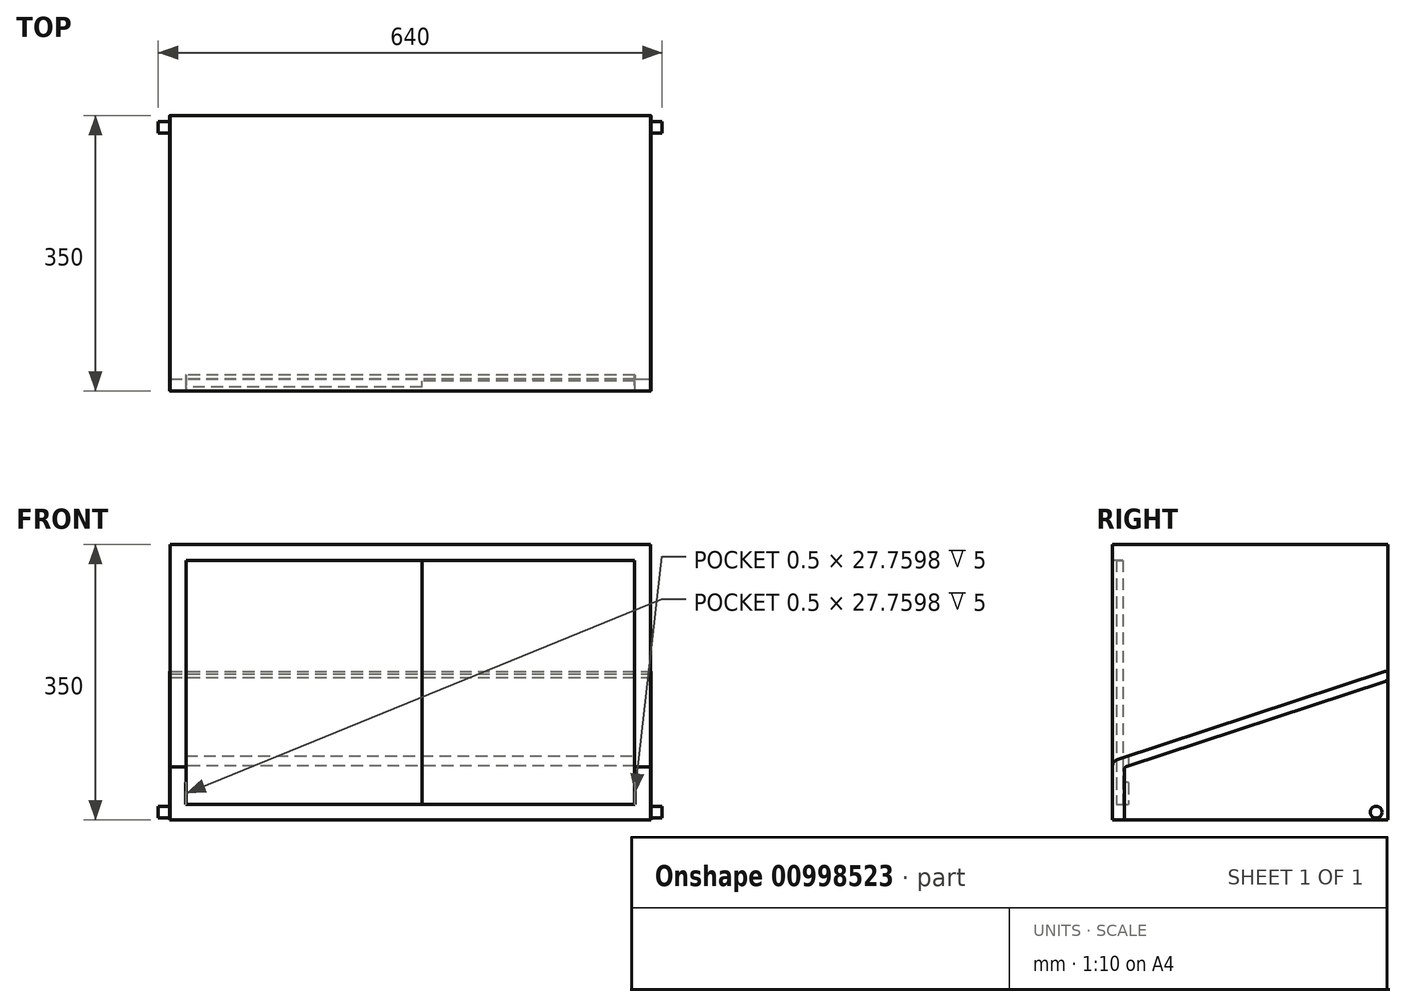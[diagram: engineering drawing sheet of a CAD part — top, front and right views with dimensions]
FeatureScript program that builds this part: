
annotation { "Feature Type Name" : "Feature", "Feature Type Description" : "" }
export const myFeature = defineFeature(function(context is Context, id is Id, definition is map)
    precondition{}
    {
        {
            var Q0;
            Q0=qCreatedBy(makeId("Right.planeOp"),FACE);
            var sketch = newSketch(context, id + "F0", { "sketchPlane" : qUnion([Q0])});
            skLineSegment(sketch, "E0.bottom", {"start": v(0, 0) * mm, "end": v(-350, 0) * mm});
            skLineSegment(sketch, "E0.top", {"start": v(0, 350) * mm, "end": v(-350, 350) * mm});
            skLineSegment(sketch, "E0.left", {"start": v(0, 0) * mm, "end": v(0, 350) * mm});
            skLineSegment(sketch, "E0.right", {"start": v(-350, 0) * mm, "end": v(-350, 350) * mm});
            skPoint(sketch, "E0.middle", {"position": v(-175, 175) * mm});
            skLineSegment(sketch, "E1", {"start": v(-350, 0) * mm, "end": v(-350, 67.76) * mm});
            skLineSegment(sketch, "E2", {"start": v(-343.12, 77.26) * mm, "end": v(-3.94, 188.7) * mm});
            skLineSegment(sketch, "E3", {"start": v(0, 185.86) * mm, "end": v(0, 180.99) * mm});
            skLineSegment(sketch, "E4", {"start": v(-3.44, 176.24) * mm, "end": v(-331.56, 68.43) * mm});
            skLineSegment(sketch, "E5", {"start": v(-335, 63.68) * mm, "end": v(-335, 0) * mm});
            skLineSegment(sketch, "E6", {"start": v(-335, 0) * mm, "end": v(-350, 0) * mm});
            skPoint(sketch, "E7.visualSharp", {"position": v(-350, 75) * mm});
            skArc(sketch, "E7.filletArc", {"start": v(-343.12, 77.26) * mm, "mid": v(-348.1, 73.62) * mm, "end": v(-350, 67.76) * mm});
            skPoint(sketch, "E8.visualSharp", {"position": v(-335, 67.3) * mm});
            skArc(sketch, "E8.filletArc", {"start": v(-331.56, 68.43) * mm, "mid": v(-334.05, 66.6) * mm, "end": v(-335, 63.68) * mm});
            skPoint(sketch, "E9.visualSharp", {"position": v(0, 177.37) * mm});
            skArc(sketch, "E9.filletArc", {"start": v(-3.44, 176.24) * mm, "mid": v(-0.95, 178.06) * mm, "end": v(0, 180.99) * mm});
            skPoint(sketch, "E10.visualSharp", {"position": v(0, 190) * mm});
            skArc(sketch, "E10.filletArc", {"start": v(0, 185.86) * mm, "mid": v(-1.24, 188.29) * mm, "end": v(-3.94, 188.7) * mm});
            skSolve(sketch);
        }
        {
            var Q0;
            {var subQ0=sQuery(id+"F0.wireOp",EDGE,"E0.bottom");Q0=makeQuery(id+"F0.imprint","IMPRINT",FACE,{"disambiguationData":[TD([[makeQuery(id+"F0.imprint","IMPRINT",EDGE,{"derivedFrom":subQ0}),-1.0]])]});}
            var Q1;
            {var subQ5=sQuery(id+"F0.wireOp",EDGE,"E6");Q1=makeQuery(id+"F0.imprint","IMPRINT",FACE,{"disambiguationData":[TD([[makeQuery(id+"F0.imprint","IMPRINT",EDGE,{"derivedFrom":subQ5}),-1.0]])]});}
            var Q2;
            {var subQ1=sQuery(id+"F0.wireOp",EDGE,"E0.top");Q2=makeQuery(id+"F0.imprint","IMPRINT",FACE,{"disambiguationData":[TD([[makeQuery(id+"F0.imprint","IMPRINT",EDGE,{"derivedFrom":subQ1}),1.0]])]});}
            extrude(context, id + "F1", {"entities" : qUnion([Q0, Q1, Q2]), "depth" : 305 * mm, "offsetDistance" : 25 * mm});
        }
        {
            var Q0;
            Q0=makeQuery(id+"F1.opExtrude","CAP_FACE",FACE,{"disambiguationData":[OSD([sQuery(id+"F0.wireOp",EDGE,"E0.bottom"),sQuery(id+"F0.wireOp",EDGE,"E0.top"),sQuery(id+"F0.wireOp",EDGE,"E0.left"),sQuery(id+"F0.wireOp",EDGE,"E1"),sQuery(id+"F0.wireOp",EDGE,"E6")])],"isStart":false});
            var sketch = newSketch(context, id + "F2", { "sketchPlane" : qUnion([Q0])});
            skLineSegment(sketch, "E11.0.0", {"start": v(-3.94, 188.7) * mm, "end": v(-343.12, 77.26) * mm});
            skArc(sketch, "E11.0.1", {"start": v(-343.12, 77.26) * mm, "mid": v(-348.1, 73.62) * mm, "end": v(-350, 67.76) * mm});
            skLineSegment(sketch, "E11.0.2", {"start": v(-350, 67.76) * mm, "end": v(-350, 67.76) * mm});
            skLineSegment(sketch, "E11.0.4", {"start": v(-335, 63.68) * mm, "end": v(-335, 63.68) * mm});
            skArc(sketch, "E11.0.5", {"start": v(-335, 63.68) * mm, "mid": v(-334.05, 66.6) * mm, "end": v(-331.56, 68.43) * mm});
            skLineSegment(sketch, "E11.0.6", {"start": v(-331.56, 68.43) * mm, "end": v(-3.44, 176.24) * mm});
            skArc(sketch, "E11.0.7", {"start": v(-3.44, 176.24) * mm, "mid": v(-0.95, 178.06) * mm, "end": v(0, 180.99) * mm});
            skLineSegment(sketch, "E11.0.8", {"start": v(0, 180.99) * mm, "end": v(0, 185.86) * mm});
            skArc(sketch, "E11.0.9", {"start": v(0, 185.86) * mm, "mid": v(-1.24, 188.29) * mm, "end": v(-3.94, 188.7) * mm});
            skLineSegment(sketch, "E11.1.0", {"start": v(-350, 0) * mm, "end": v(-335, 0) * mm});
            skLineSegment(sketch, "E11.1.1", {"start": v(-335, 0) * mm, "end": v(-335, 63.68) * mm});
            skLineSegment(sketch, "E11.1.3", {"start": v(-350, 67.76) * mm, "end": v(-350, 0) * mm});
            skSolve(sketch);
        }
        {
            var Q0;
            Q0=qSketchRegion(id+"F2",true);
            extrude(context, id + "F3", {"entities" : qUnion([Q0]), "depth" : 0.5 * mm, "offsetDistance" : 25 * mm});
        }
        {
            var Q0;
            Q0=makeQuery(id+"F1.opExtrude","CAP_FACE",FACE,{"disambiguationData":[OSD([sQuery(id+"F0.wireOp",EDGE,"E0.bottom"),sQuery(id+"F0.wireOp",EDGE,"E0.top"),sQuery(id+"F0.wireOp",EDGE,"E0.left"),sQuery(id+"F0.wireOp",EDGE,"E1"),sQuery(id+"F0.wireOp",EDGE,"E6")])],"isStart":false});
            var sketch = newSketch(context, id + "F4", { "sketchPlane" : qUnion([Q0])});
            skLineSegment(sketch, "E12", {"start": v(-30, 350) * mm, "end": v(-30, 0) * mm, "construction": true});
            skLineSegment(sketch, "E13", {"start": v(-30, 10) * mm, "end": v(0, 10) * mm, "construction": true});
            skCircle(sketch, "E14", {"center": v(-15, 10) * mm, "radius": 7.5 * mm});
            skSolve(sketch);
        }
        {
            var Q0;
            Q0=qSketchRegion(id+"F4",true);
            extrude(context, id + "F5", {"entities" : qUnion([Q0]), "operationType" : NewBodyOperationType.ADD, "depth" : 15 * mm, "offsetDistance" : 25 * mm});
        }
        {
            var Q0;
            Q0=makeQuery(id+"F1.opExtrude","SWEPT_BODY",BODY,{"disambiguationData":[OSD([sQuery(id+"F0.wireOp",EDGE,"E0.bottom"),sQuery(id+"F0.wireOp",EDGE,"E0.top"),sQuery(id+"F0.wireOp",EDGE,"E0.left"),sQuery(id+"F0.wireOp",EDGE,"E1"),sQuery(id+"F0.wireOp",EDGE,"E6")])]});
            var Q1;
            Q1=makeQuery(id+"F3.opExtrude","SWEPT_BODY",BODY,{"disambiguationData":[OSD([sQuery(id+"F2.wireOp",EDGE,"E11.0.0"),sQuery(id+"F2.wireOp",EDGE,"E11.0.1"),sQuery(id+"F2.wireOp",EDGE,"E11.0.2"),sQuery(id+"F2.wireOp",EDGE,"E11.0.4"),sQuery(id+"F2.wireOp",EDGE,"E11.0.5"),sQuery(id+"F2.wireOp",EDGE,"E11.0.6"),sQuery(id+"F2.wireOp",EDGE,"E11.0.7"),sQuery(id+"F2.wireOp",EDGE,"E11.0.8"),sQuery(id+"F2.wireOp",EDGE,"E11.0.9"),sQuery(id+"F2.wireOp",EDGE,"E11.1.0"),sQuery(id+"F2.wireOp",EDGE,"E11.1.1"),sQuery(id+"F2.wireOp",EDGE,"E11.1.3")])]});
            var Q2;
            Q2=qCreatedBy(makeId("Right.planeOp"),FACE);
            mirror(context, id + "F6", {"entities" : qUnion([Q0, Q1]), "mirrorPlane" : qUnion([Q2])});
        }
        {
            var Q0;
            Q0=makeQuery(id+"F6.opPattern","COPY",BODY,{"derivedFrom":makeQuery(id+"F1.opExtrude","SWEPT_BODY",BODY,{"disambiguationData":[OSD([sQuery(id+"F0.wireOp",EDGE,"E0.bottom"),sQuery(id+"F0.wireOp",EDGE,"E0.top"),sQuery(id+"F0.wireOp",EDGE,"E0.left"),sQuery(id+"F0.wireOp",EDGE,"E1"),sQuery(id+"F0.wireOp",EDGE,"E6")])]}),"instanceName":"1"});
            var Q1;
            Q1=makeQuery(id+"F1.opExtrude","SWEPT_BODY",BODY,{"disambiguationData":[OSD([sQuery(id+"F0.wireOp",EDGE,"E0.bottom"),sQuery(id+"F0.wireOp",EDGE,"E0.top"),sQuery(id+"F0.wireOp",EDGE,"E0.left"),sQuery(id+"F0.wireOp",EDGE,"E1"),sQuery(id+"F0.wireOp",EDGE,"E6")])]});
            var Q2;
            Q2=makeQuery(id+"F6.opPattern","COPY",BODY,{"derivedFrom":makeQuery(id+"F3.opExtrude","SWEPT_BODY",BODY,{"disambiguationData":[OSD([sQuery(id+"F2.wireOp",EDGE,"E11.0.0"),sQuery(id+"F2.wireOp",EDGE,"E11.0.1"),sQuery(id+"F2.wireOp",EDGE,"E11.0.2"),sQuery(id+"F2.wireOp",EDGE,"E11.0.4"),sQuery(id+"F2.wireOp",EDGE,"E11.0.5"),sQuery(id+"F2.wireOp",EDGE,"E11.0.6"),sQuery(id+"F2.wireOp",EDGE,"E11.0.7"),sQuery(id+"F2.wireOp",EDGE,"E11.0.8"),sQuery(id+"F2.wireOp",EDGE,"E11.0.9"),sQuery(id+"F2.wireOp",EDGE,"E11.1.0"),sQuery(id+"F2.wireOp",EDGE,"E11.1.1"),sQuery(id+"F2.wireOp",EDGE,"E11.1.3")])]}),"instanceName":"1"});
            var Q3;
            Q3=makeQuery(id+"F3.opExtrude","SWEPT_BODY",BODY,{"disambiguationData":[OSD([sQuery(id+"F2.wireOp",EDGE,"E11.0.0"),sQuery(id+"F2.wireOp",EDGE,"E11.0.1"),sQuery(id+"F2.wireOp",EDGE,"E11.0.2"),sQuery(id+"F2.wireOp",EDGE,"E11.0.4"),sQuery(id+"F2.wireOp",EDGE,"E11.0.5"),sQuery(id+"F2.wireOp",EDGE,"E11.0.6"),sQuery(id+"F2.wireOp",EDGE,"E11.0.7"),sQuery(id+"F2.wireOp",EDGE,"E11.0.8"),sQuery(id+"F2.wireOp",EDGE,"E11.0.9"),sQuery(id+"F2.wireOp",EDGE,"E11.1.0"),sQuery(id+"F2.wireOp",EDGE,"E11.1.1"),sQuery(id+"F2.wireOp",EDGE,"E11.1.3")])]});
            booleanBodies(context, id + "F7", {"operationType" : BooleanOperationType.UNION, "tools" : qUnion([Q0, Q1, Q2, Q3])});
        }
        {
            var Q0;
            {var subQ0=makeQuery(id+"F3.opExtrude","SWEPT_FACE",FACE,{"disambiguationData":[OSD([sQuery(id+"F2.wireOp",EDGE,"E11.1.3")])]});var subQ1=makeQuery(id+"F1.opExtrude","SWEPT_FACE",FACE,{"disambiguationData":[OSD([sQuery(id+"F0.wireOp",EDGE,"E0.right"),sQuery(id+"F0.wireOp",EDGE,"E1")])]});Q0=makeQuery(id+"F7.opBoolean","MERGE",FACE,{"derivedFrom":[subQ1,subQ0,makeQuery(id+"F6.opPattern","COPY",FACE,{"derivedFrom":subQ1,"instanceName":"1"}),makeQuery(id+"F6.opPattern","COPY",FACE,{"derivedFrom":subQ0,"instanceName":"1"})]});}
            var sketch = newSketch(context, id + "F8", { "sketchPlane" : qUnion([Q0])});
            skLineSegment(sketch, "E15.0", {"start": v(-285.5, 47.76) * mm, "end": v(-285.5, 20) * mm});
            skLineSegment(sketch, "E15.1", {"start": v(-285, 47.76) * mm, "end": v(-285.5, 47.76) * mm});
            skLineSegment(sketch, "E15.2", {"start": v(-285.5, 20) * mm, "end": v(285.5, 20) * mm});
            skLineSegment(sketch, "E15.3", {"start": v(-285, 330) * mm, "end": v(-285, 47.76) * mm});
            skLineSegment(sketch, "E15.4", {"start": v(285.5, 20) * mm, "end": v(285.5, 47.76) * mm});
            skLineSegment(sketch, "E15.5", {"start": v(285.5, 47.76) * mm, "end": v(285, 47.76) * mm});
            skLineSegment(sketch, "E15.6", {"start": v(285, 47.76) * mm, "end": v(285, 330) * mm});
            skLineSegment(sketch, "E15.7", {"start": v(285, 330) * mm, "end": v(-285, 330) * mm});
            skSolve(sketch);
        }
        {
            var Q0;
            Q0 = qSketchRegion(id + "F8", true);
            extrude(context, id + "F9", {"entities" : qUnion([Q0]), "operationType" : NewBodyOperationType.REMOVE, "oppositeDirection" : true, "depth" : 20 * mm, "offsetDistance" : 25 * mm});
        }
        {
            var Q0;
            Q0=makeQuery(id+"F9.boolean.opBoolean","COPY",FACE,{"derivedFrom":makeQuery(id+"F9.opExtrude","CAP_FACE",FACE,{"disambiguationData":[OSD([sQuery(id+"F8.wireOp",EDGE,"E15.0"),sQuery(id+"F8.wireOp",EDGE,"E15.1"),sQuery(id+"F8.wireOp",EDGE,"E15.2"),sQuery(id+"F8.wireOp",EDGE,"E15.3"),sQuery(id+"F8.wireOp",EDGE,"E15.4"),sQuery(id+"F8.wireOp",EDGE,"E15.5"),sQuery(id+"F8.wireOp",EDGE,"E15.6"),sQuery(id+"F8.wireOp",EDGE,"E15.7")])],"isStart":false})});
            var sketch = newSketch(context, id + "F10", { "sketchPlane" : qUnion([Q0])});
            skLineSegment(sketch, "E16.bottom", {"start": v(-285, 330) * mm, "end": v(15, 330) * mm});
            skLineSegment(sketch, "E16.top", {"start": v(-285, 20) * mm, "end": v(15, 20) * mm});
            skLineSegment(sketch, "E16.left", {"start": v(-285, 330) * mm, "end": v(-285, 20) * mm});
            skLineSegment(sketch, "E16.right", {"start": v(15, 330) * mm, "end": v(15, 20) * mm});
            skPoint(sketch, "E16.middle", {"position": v(-135, 175) * mm});
            skSolve(sketch);
        }
        {
            var Q0;
            Q0 = qSketchRegion(id + "F10", true);
            extrude(context, id + "F11", {"entities" : qUnion([Q0]), "depth" : 15 * mm, "offsetDistance" : 25 * mm});
        }
        {
            var Q0;
            Q0=makeQuery(id+"F9.boolean.opBoolean","COPY",FACE,{"derivedFrom":makeQuery(id+"F9.opExtrude","CAP_FACE",FACE,{"disambiguationData":[OSD([sQuery(id+"F8.wireOp",EDGE,"E15.0"),sQuery(id+"F8.wireOp",EDGE,"E15.1"),sQuery(id+"F8.wireOp",EDGE,"E15.2"),sQuery(id+"F8.wireOp",EDGE,"E15.3"),sQuery(id+"F8.wireOp",EDGE,"E15.4"),sQuery(id+"F8.wireOp",EDGE,"E15.5"),sQuery(id+"F8.wireOp",EDGE,"E15.6"),sQuery(id+"F8.wireOp",EDGE,"E15.7")])],"isStart":false})});
            var sketch = newSketch(context, id + "F12", { "sketchPlane" : qUnion([Q0])});
            skLineSegment(sketch, "E17.bottom", {"start": v(-15, 330) * mm, "end": v(285, 330) * mm});
            skLineSegment(sketch, "E17.top", {"start": v(-15, 20) * mm, "end": v(285, 20) * mm});
            skLineSegment(sketch, "E17.left", {"start": v(-15, 330) * mm, "end": v(-15, 20) * mm});
            skLineSegment(sketch, "E17.right", {"start": v(285, 330) * mm, "end": v(285, 20) * mm});
            skPoint(sketch, "E17.middle", {"position": v(135, 175) * mm});
            skSolve(sketch);
        }
        {
            var Q0;
            Q0 = qSketchRegion(id + "F12", true);
            extrude(context, id + "F13", {"entities" : qUnion([Q0]), "operationType" : NewBodyOperationType.ADD, "depth" : 7 * mm, "offsetDistance" : 25 * mm});
        }
    });
